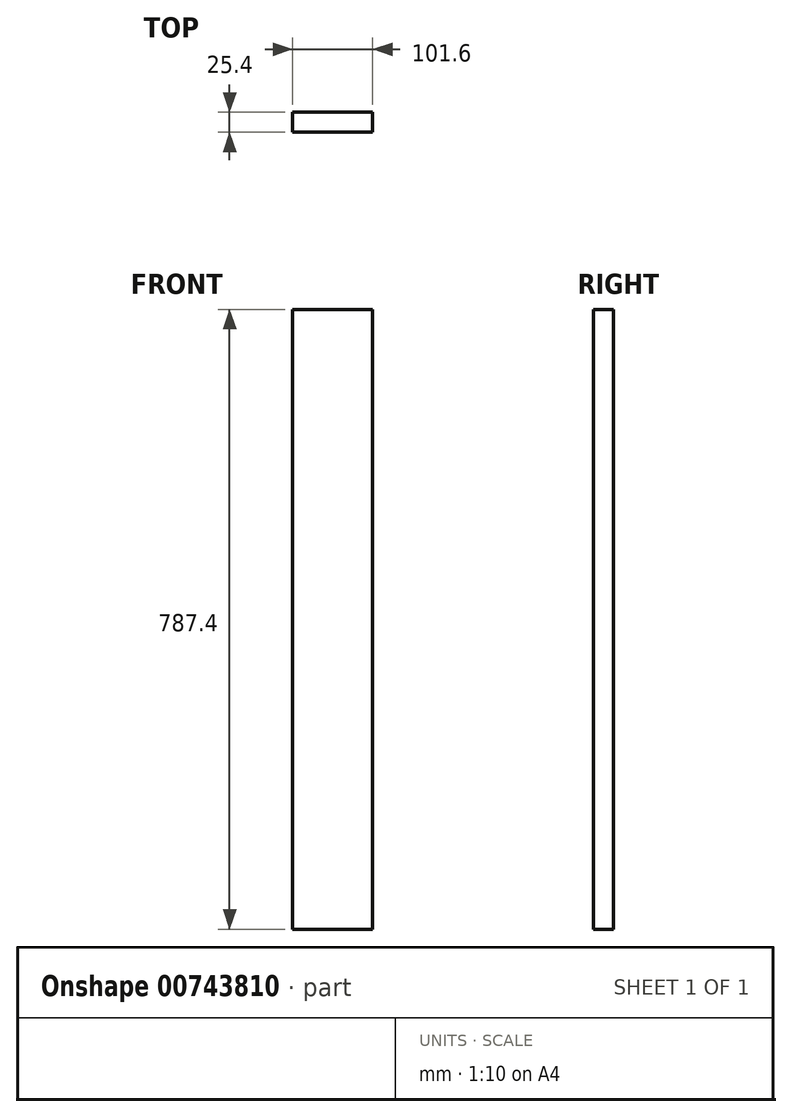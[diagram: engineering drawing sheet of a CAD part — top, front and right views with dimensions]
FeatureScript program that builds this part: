
annotation { "Feature Type Name" : "Feature", "Feature Type Description" : "" }
export const myFeature = defineFeature(function(context is Context, id is Id, definition is map)
    precondition{}
    {
        {
            var Q0;
            Q0=qCreatedBy(makeId("Front.planeOp"),FACE);
            var sketch = newSketch(context, id + "F0", { "sketchPlane" : qUnion([Q0])});
            skLineSegment(sketch, "E0.bottom", {"start": v(50.8, 393.7) * mm, "end": v(-50.8, 393.7) * mm});
            skLineSegment(sketch, "E0.top", {"start": v(50.8, -393.7) * mm, "end": v(-50.8, -393.7) * mm});
            skLineSegment(sketch, "E0.left", {"start": v(50.8, 393.7) * mm, "end": v(50.8, -393.7) * mm});
            skLineSegment(sketch, "E0.right", {"start": v(-50.8, 393.7) * mm, "end": v(-50.8, -393.7) * mm});
            skPoint(sketch, "E0.middle", {"position": v(0, 0) * mm});
            skSolve(sketch);
        }
        {
            var Q0;
            Q0=makeQuery(id+"F0.imprint","IMPRINT",FACE,{"disambiguationData":[TD([[makeQuery(id+"F0.imprint","IMPRINT",EDGE,{"derivedFrom":sQuery(id+"F0.wireOp",EDGE,"E0.bottom")}),1.0]])]});
            extrude(context, id + "F1", {"entities" : qUnion([Q0]), "depth" : 25.4 * mm, "offsetDistance" : 25.4 * mm});
        }
    });
